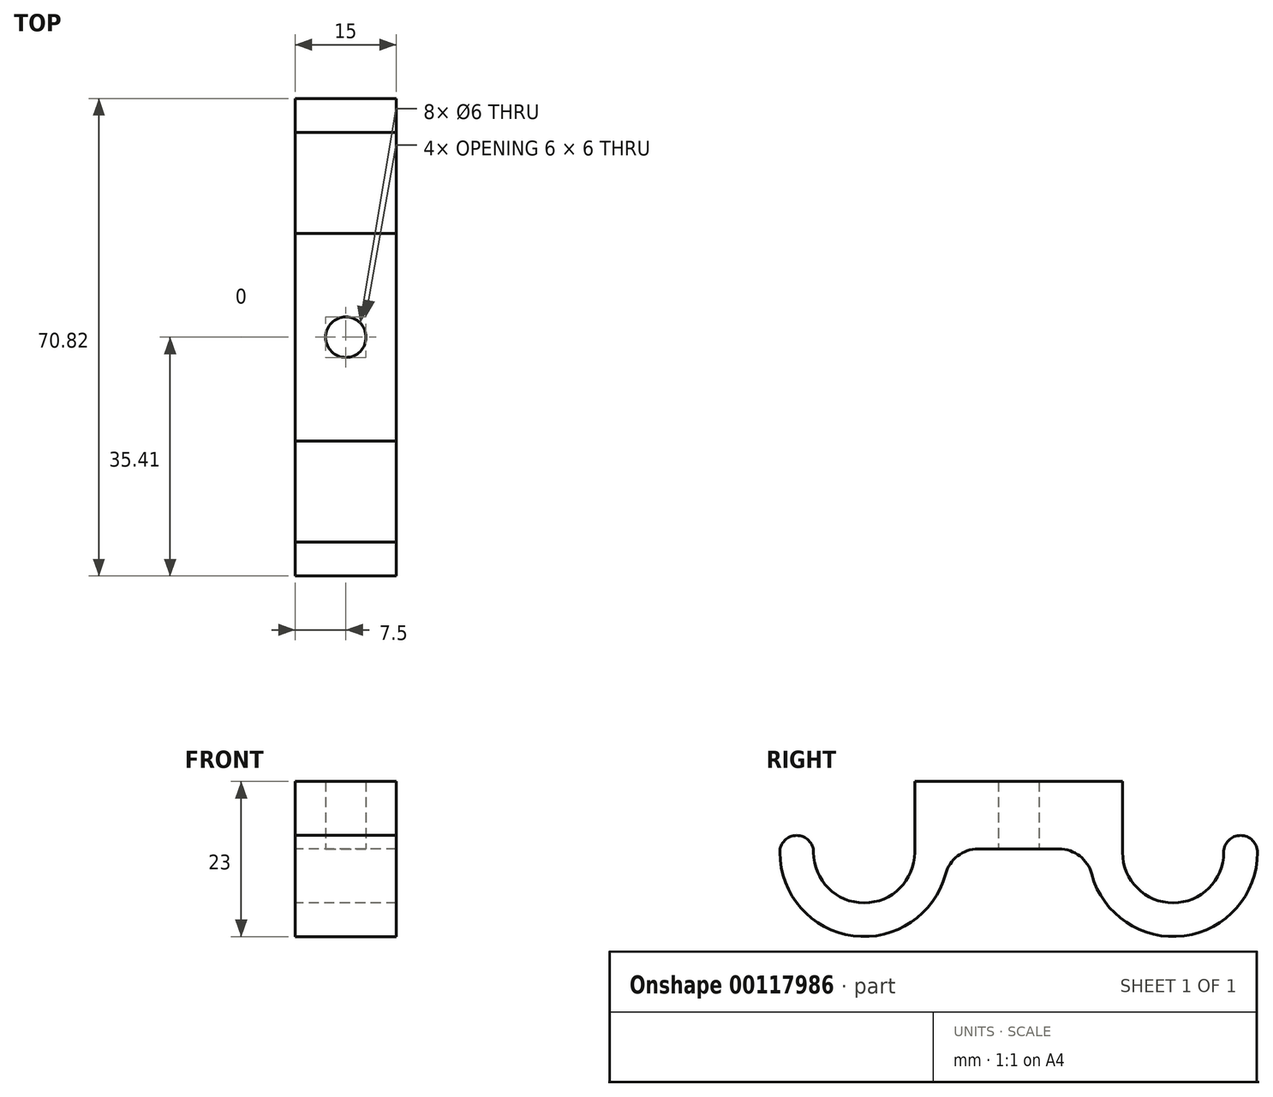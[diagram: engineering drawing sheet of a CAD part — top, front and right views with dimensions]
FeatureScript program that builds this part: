
annotation { "Feature Type Name" : "Feature", "Feature Type Description" : "" }
export const myFeature = defineFeature(function(context is Context, id is Id, definition is map)
    precondition{}
    {
        {
            var Q0;
            Q0=qCreatedBy(makeId("Right.planeOp"),FACE);
            var sketch = newSketch(context, id + "F0", { "sketchPlane" : qUnion([Q0])});
            skLineSegment(sketch, "E0.bottom", {"start": v(-15.41, 0) * mm, "end": v(15.41, 0) * mm});
            skLineSegment(sketch, "E0.top", {"start": v(-6, -10) * mm, "end": v(6, -10) * mm});
            skLineSegment(sketch, "E0.left", {"start": v(-15.41, 0) * mm, "end": v(-15.41, -10.5) * mm});
            skLineSegment(sketch, "E0.right", {"start": v(15.41, 0) * mm, "end": v(15.41, -10.5) * mm});
            skPoint(sketch, "E0.middle", {"position": v(0, 0) * mm});
            skArc(sketch, "E1", {"start": v(15.41, -10.5) * mm, "mid": v(22.91, -18) * mm, "end": v(30.41, -10.5) * mm});
            skArc(sketch, "E2", {"start": v(10.83, -13.71) * mm, "mid": v(24.53, -22.9) * mm, "end": v(35.41, -10.5) * mm});
            skArc(sketch, "E3", {"start": v(35.41, -10.5) * mm, "mid": v(32.91, -8) * mm, "end": v(30.41, -10.5) * mm});
            skArc(sketch, "E4.MirrorCS", {"start": v(-35.41, -10.5) * mm, "mid": v(-32.91, -8) * mm, "end": v(-30.41, -10.5) * mm});
            skArc(sketch, "E5.MirrorCS", {"start": v(-15.41, -10.5) * mm, "mid": v(-22.91, -18) * mm, "end": v(-30.41, -10.5) * mm});
            skArc(sketch, "E6.MirrorCS", {"start": v(-10.83, -13.71) * mm, "mid": v(-24.53, -22.9) * mm, "end": v(-35.41, -10.5) * mm});
            skArc(sketch, "E7.filletArc", {"start": v(10.83, -13.71) * mm, "mid": v(9.05, -11.04) * mm, "end": v(6, -10) * mm});
            skArc(sketch, "E8.filletArc", {"start": v(-6, -10) * mm, "mid": v(-9.05, -11.04) * mm, "end": v(-10.83, -13.71) * mm});
            skSolve(sketch);
        }
        {
            var Q0;
            {var subQ0=sQuery(id+"F0.wireOp",EDGE,"E0.bottom");Q0=makeQuery(id+"F0.imprint","IMPRINT",FACE,{"disambiguationData":[TD([[makeQuery(id+"F0.imprint","IMPRINT",EDGE,{"derivedFrom":subQ0}),-1.0]])]});}
            extrude(context, id + "F1", {"entities" : qUnion([Q0]), "depth" : 15 * mm});
        }
        {
            var Q0;
            Q0=makeQuery(id+"F1.opExtrude","SWEPT_FACE",FACE,{"disambiguationData":[OSD([sQuery(id+"F0.wireOp",EDGE,"E0.top")])]});
            var sketch = newSketch(context, id + "F2", { "sketchPlane" : qUnion([Q0])});
            skCircle(sketch, "E9", {"center": v(7.5, 0) * mm, "radius": 3 * mm});
            skLineSegment(sketch, "E10", {"start": v(0, 0) * mm, "end": v(15, 0) * mm, "construction": true});
            skSolve(sketch);
        }
        {
            var Q0;
            Q0=makeQuery(id+"F2.imprint","IMPRINT",FACE,{"disambiguationData":[TD([[makeQuery(id+"F2.imprint","IMPRINT",EDGE,{"derivedFrom":sQuery(id+"F2.wireOp",EDGE,"E9")}),1.0]])]});
            extrude(context, id + "F3", {"entities" : qUnion([Q0]), "operationType" : NewBodyOperationType.REMOVE, "endBound" : BoundingType.UP_TO_NEXT, "oppositeDirection" : true, "depth" : 25 * mm});
        }
    });
